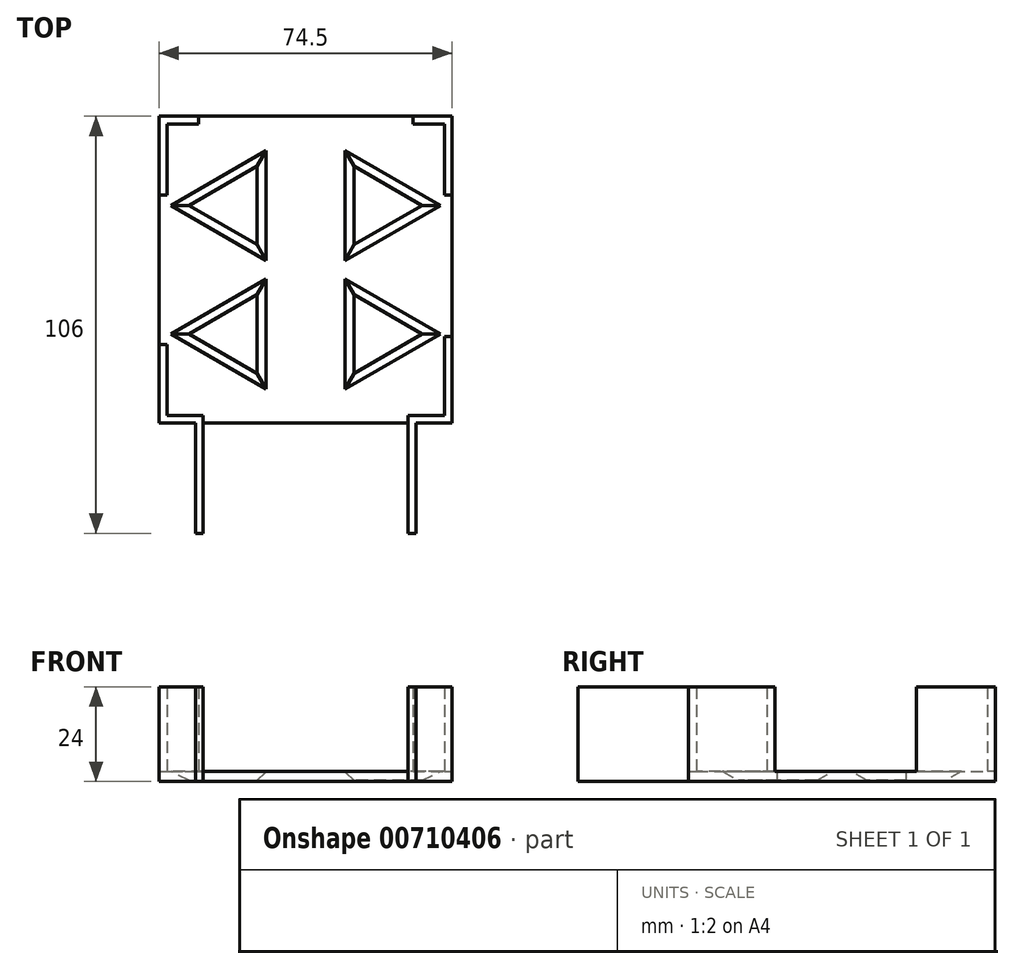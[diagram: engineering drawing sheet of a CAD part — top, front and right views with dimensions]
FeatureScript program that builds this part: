
annotation { "Feature Type Name" : "Feature", "Feature Type Description" : "" }
export const myFeature = defineFeature(function(context is Context, id is Id, definition is map)
    precondition{}
    {
        {
            var Q0;
            Q0=qCreatedBy(makeId("Top.planeOp"),FACE);
            var sketch = newSketch(context, id + "F0", { "sketchPlane" : qUnion([Q0])});
            skLineSegment(sketch, "E0.bottom", {"start": v(-37.25, -39) * mm, "end": v(37.25, -39) * mm});
            skLineSegment(sketch, "E0.top", {"start": v(-37.25, 39) * mm, "end": v(37.25, 39) * mm});
            skLineSegment(sketch, "E0.left", {"start": v(-37.25, -39) * mm, "end": v(-37.25, 39) * mm});
            skLineSegment(sketch, "E0.right", {"start": v(37.25, -39) * mm, "end": v(37.25, 39) * mm});
            skPoint(sketch, "E0.middle", {"position": v(0, 0) * mm});
            skLineSegment(sketch, "E1", {"start": v(0, -39) * mm, "end": v(0, 39) * mm});
            skLineSegment(sketch, "E2", {"start": v(29.62, 16.33) * mm, "end": v(12.3, 6.33) * mm});
            skLineSegment(sketch, "E3", {"start": v(12.3, 6.33) * mm, "end": v(12.3, 26.33) * mm});
            skLineSegment(sketch, "E4", {"start": v(12.3, 26.33) * mm, "end": v(29.62, 16.33) * mm});
            skLineSegment(sketch, "E5.MirrorCS", {"start": v(-12.3, 6.33) * mm, "end": v(-12.3, 26.33) * mm});
            skLineSegment(sketch, "E6.MirrorCS", {"start": v(-12.3, 26.33) * mm, "end": v(-29.62, 16.33) * mm});
            skLineSegment(sketch, "E7.MirrorCS", {"start": v(-29.62, 16.33) * mm, "end": v(-12.3, 6.33) * mm});
            skLineSegment(sketch, "E8.MirrorCS", {"start": v(-29.62, -16.33) * mm, "end": v(-12.3, -6.33) * mm});
            skLineSegment(sketch, "E9.MirrorCS", {"start": v(-12.3, -26.33) * mm, "end": v(-29.62, -16.33) * mm});
            skLineSegment(sketch, "E10.MirrorCS", {"start": v(-12.3, -6.33) * mm, "end": v(-12.3, -26.33) * mm});
            skLineSegment(sketch, "E11.MirrorCS", {"start": v(12.3, -6.33) * mm, "end": v(12.3, -26.33) * mm});
            skLineSegment(sketch, "E12.MirrorCS", {"start": v(12.3, -26.33) * mm, "end": v(29.62, -16.33) * mm});
            skLineSegment(sketch, "E13.MirrorCS", {"start": v(29.62, -16.33) * mm, "end": v(12.3, -6.33) * mm});
            skLineSegment(sketch, "E14", {"start": v(-35.25, 37) * mm, "end": v(35.25, 37) * mm});
            skLineSegment(sketch, "E15", {"start": v(35.25, 37) * mm, "end": v(35.25, -37) * mm});
            skLineSegment(sketch, "E16", {"start": v(35.25, -37) * mm, "end": v(-35.25, -37) * mm});
            skLineSegment(sketch, "E17", {"start": v(-35.25, -37) * mm, "end": v(-35.25, 37) * mm});
            skLineSegment(sketch, "E18", {"start": v(37.25, 39) * mm, "end": v(37.25, 19) * mm, "construction": true});
            skLineSegment(sketch, "E19", {"start": v(37.25, 19) * mm, "end": v(35.25, 19) * mm});
            skLineSegment(sketch, "E20", {"start": v(37.25, 39) * mm, "end": v(27.25, 39) * mm, "construction": true});
            skLineSegment(sketch, "E21", {"start": v(27.25, 39) * mm, "end": v(27.25, 37) * mm});
            skLineSegment(sketch, "E22", {"start": v(35.25, -37) * mm, "end": v(35.25, -17) * mm, "construction": true});
            skLineSegment(sketch, "E23", {"start": v(35.25, -17) * mm, "end": v(37.25, -17) * mm});
            skLineSegment(sketch, "E24", {"start": v(-37.25, 39) * mm, "end": v(-37.25, 19) * mm, "construction": true});
            skLineSegment(sketch, "E25", {"start": v(-37.25, 19) * mm, "end": v(-35.25, 19) * mm});
            skLineSegment(sketch, "E26", {"start": v(37.25, -39) * mm, "end": v(28, -39) * mm, "construction": true});
            skLineSegment(sketch, "E27", {"start": v(26, -39) * mm, "end": v(26, -37) * mm});
            skLineSegment(sketch, "E28", {"start": v(-37.25, -39) * mm, "end": v(-28, -39) * mm, "construction": true});
            skLineSegment(sketch, "E29", {"start": v(-26, -39) * mm, "end": v(-26, -37) * mm});
            skLineSegment(sketch, "E30", {"start": v(-37.25, -39) * mm, "end": v(-37.25, -19) * mm, "construction": true});
            skLineSegment(sketch, "E31", {"start": v(-37.25, -19) * mm, "end": v(-35.25, -19) * mm});
            skLineSegment(sketch, "E32", {"start": v(-37.25, 39) * mm, "end": v(-27.25, 39) * mm, "construction": true});
            skLineSegment(sketch, "E33", {"start": v(-27.25, 39) * mm, "end": v(-27.25, 37) * mm});
            skText(sketch, "E34", { "text": "Front", "fontName": "OpenSans-Italic.ttf"});
            skText(sketch, "E35", { "text": "Back", "fontName": "OpenSans-Italic.ttf"});
            skLineSegment(sketch, "E36", {"start": v(28, -39) * mm, "end": v(28, -67) * mm});
            skLineSegment(sketch, "E37", {"start": v(-28, -39) * mm, "end": v(-28, -67) * mm});
            skLineSegment(sketch, "E38", {"start": v(28, -67) * mm, "end": v(26, -67) * mm});
            skLineSegment(sketch, "E39", {"start": v(26, -67) * mm, "end": v(26, -39) * mm});
            skLineSegment(sketch, "E40", {"start": v(-28, -67) * mm, "end": v(-26, -67) * mm});
            skLineSegment(sketch, "E41", {"start": v(-26, -67) * mm, "end": v(-26, -39) * mm});
            const initialGuessF0  = {"E34": [-0.01968, 0.05832, 1, 0, 0.01165], "E35": [-0.01674, -0.07005, 1, 0, 0.0123]};
            skSetInitialGuess(sketch, initialGuessF0);
            skSolve(sketch);
        }
        {
            var Q0;
            Q0=makeQuery(id+"F0.imprint","IMPRINT",FACE,{"disambiguationData":[TD([[makeQuery(id+"F0.imprint","IMPRINT",EDGE,{"derivedFrom":sQuery(id+"F0.wireOp",EDGE,"E2")}),1.0]])]});
            var Q1;
            Q1=makeQuery(id+"F0.imprint","IMPRINT",FACE,{"disambiguationData":[TD([[makeQuery(id+"F0.imprint","IMPRINT",EDGE,{"derivedFrom":sQuery(id+"F0.wireOp",EDGE,"E5.MirrorCS")}),-1.0]])]});
            var Q2;
            {var subQ3=sQuery(id+"F0.wireOp",EDGE,"E29");Q2=makeQuery(id+"F0.imprint","IMPRINT",FACE,{"disambiguationData":[TD([[makeQuery(id+"F0.imprint","IMPRINT",EDGE,{"derivedFrom":subQ3}),-1.0]])]});}
            var Q3;
            {var subQ3=sQuery(id+"F0.wireOp",EDGE,"E27");Q3=makeQuery(id+"F0.imprint","IMPRINT",FACE,{"disambiguationData":[TD([[makeQuery(id+"F0.imprint","IMPRINT",EDGE,{"derivedFrom":subQ3}),1.0]])]});}
            var Q4;
            {var subQ3=sQuery(id+"F0.wireOp",EDGE,"E33");Q4=makeQuery(id+"F0.imprint","IMPRINT",FACE,{"disambiguationData":[TD([[makeQuery(id+"F0.imprint","IMPRINT",EDGE,{"derivedFrom":subQ3}),1.0]])]});}
            var Q5;
            {var subQ3=sQuery(id+"F0.wireOp",EDGE,"E21");Q5=makeQuery(id+"F0.imprint","IMPRINT",FACE,{"disambiguationData":[TD([[makeQuery(id+"F0.imprint","IMPRINT",EDGE,{"derivedFrom":subQ3}),-1.0]])]});}
            var Q6;
            {var subQ0=sQuery(id+"F0.wireOp",EDGE,"E19");Q6=makeQuery(id+"F0.imprint","IMPRINT",FACE,{"disambiguationData":[TD([[makeQuery(id+"F0.imprint","IMPRINT",EDGE,{"derivedFrom":subQ0}),1.0]])]});}
            var Q7;
            {var subQ0=sQuery(id+"F0.wireOp",EDGE,"E25");Q7=makeQuery(id+"F0.imprint","IMPRINT",FACE,{"disambiguationData":[TD([[makeQuery(id+"F0.imprint","IMPRINT",EDGE,{"derivedFrom":subQ0}),-1.0]])]});}
            extrude(context, id + "F1", {"entities" : qUnion([Q0, Q1, Q2, Q3, Q4, Q5, Q6, Q7]), "depth" : 2.5 * mm, "offsetDistance" : 25 * mm});
        }
        {
            var Q0;
            Q0=makeQuery(id+"F1.opExtrude","CAP_EDGE",EDGE,{"disambiguationData":[OSD([sQuery(id+"F0.wireOp",EDGE,"E8.MirrorCS")])],"isStart":false});
            var Q1;
            Q1=makeQuery(id+"F1.opExtrude","CAP_EDGE",EDGE,{"disambiguationData":[OSD([sQuery(id+"F0.wireOp",EDGE,"E9.MirrorCS")])],"isStart":false});
            var Q2;
            Q2=makeQuery(id+"F1.opExtrude","CAP_EDGE",EDGE,{"disambiguationData":[OSD([sQuery(id+"F0.wireOp",EDGE,"E10.MirrorCS")])],"isStart":false});
            var Q3;
            Q3=makeQuery(id+"F1.opExtrude","CAP_EDGE",EDGE,{"disambiguationData":[OSD([sQuery(id+"F0.wireOp",EDGE,"E13.MirrorCS")])],"isStart":false});
            var Q4;
            Q4=makeQuery(id+"F1.opExtrude","CAP_EDGE",EDGE,{"disambiguationData":[OSD([sQuery(id+"F0.wireOp",EDGE,"E11.MirrorCS")])],"isStart":false});
            var Q5;
            Q5=makeQuery(id+"F1.opExtrude","CAP_EDGE",EDGE,{"disambiguationData":[OSD([sQuery(id+"F0.wireOp",EDGE,"E12.MirrorCS")])],"isStart":false});
            var Q6;
            Q6=makeQuery(id+"F1.opExtrude","CAP_EDGE",EDGE,{"disambiguationData":[OSD([sQuery(id+"F0.wireOp",EDGE,"E4")])],"isStart":false});
            var Q7;
            Q7=makeQuery(id+"F1.opExtrude","CAP_EDGE",EDGE,{"disambiguationData":[OSD([sQuery(id+"F0.wireOp",EDGE,"E3")])],"isStart":false});
            var Q8;
            Q8=makeQuery(id+"F1.opExtrude","CAP_EDGE",EDGE,{"disambiguationData":[OSD([sQuery(id+"F0.wireOp",EDGE,"E2")])],"isStart":false});
            var Q9;
            Q9=makeQuery(id+"F1.opExtrude","CAP_EDGE",EDGE,{"disambiguationData":[OSD([sQuery(id+"F0.wireOp",EDGE,"E6.MirrorCS")])],"isStart":false});
            var Q10;
            Q10=makeQuery(id+"F1.opExtrude","CAP_EDGE",EDGE,{"disambiguationData":[OSD([sQuery(id+"F0.wireOp",EDGE,"E7.MirrorCS")])],"isStart":false});
            var Q11;
            Q11=makeQuery(id+"F1.opExtrude","CAP_EDGE",EDGE,{"disambiguationData":[OSD([sQuery(id+"F0.wireOp",EDGE,"E5.MirrorCS")])],"isStart":false});
            chamfer(context, id + "F2", {"entities" : qUnion([Q0, Q1, Q2, Q3, Q4, Q5, Q6, Q7, Q8, Q9, Q10, Q11]), "width" : 2.3 * mm, "tangentPropagation" : true});
        }
        {
            var Q0;
            {var subQ3=sQuery(id+"F0.wireOp",EDGE,"E25");Q0=makeQuery(id+"F0.imprint","IMPRINT",FACE,{"disambiguationData":[TD([[makeQuery(id+"F0.imprint","IMPRINT",EDGE,{"derivedFrom":subQ3}),1.0]])]});}
            var Q1;
            {var subQ3=sQuery(id+"F0.wireOp",EDGE,"E19");Q1=makeQuery(id+"F0.imprint","IMPRINT",FACE,{"disambiguationData":[TD([[makeQuery(id+"F0.imprint","IMPRINT",EDGE,{"derivedFrom":subQ3}),-1.0]])]});}
            var Q2;
            {var subQ3=sQuery(id+"F0.wireOp",EDGE,"E23");Q2=makeQuery(id+"F0.imprint","IMPRINT",FACE,{"disambiguationData":[TD([[makeQuery(id+"F0.imprint","IMPRINT",EDGE,{"derivedFrom":subQ3}),-1.0]])]});}
            var Q3;
            {var subQ3=sQuery(id+"F0.wireOp",EDGE,"E29");Q3=makeQuery(id+"F0.imprint","IMPRINT",FACE,{"disambiguationData":[TD([[makeQuery(id+"F0.imprint","IMPRINT",EDGE,{"derivedFrom":subQ3}),1.0]])]});}
            var Q4;
            {var subQ2=sQuery(id+"F0.wireOp",EDGE,"E36");Q4=makeQuery(id+"F0.imprint","IMPRINT",FACE,{"disambiguationData":[TD([[makeQuery(id+"F0.imprint","IMPRINT",EDGE,{"derivedFrom":subQ2}),-1.0]])]});}
            var Q5;
            {var subQ2=sQuery(id+"F0.wireOp",EDGE,"E37");Q5=makeQuery(id+"F0.imprint","IMPRINT",FACE,{"disambiguationData":[TD([[makeQuery(id+"F0.imprint","IMPRINT",EDGE,{"derivedFrom":subQ2}),1.0]])]});}
            extrude(context, id + "F3", {"entities" : qUnion([Q0, Q1, Q2, Q3, Q4, Q5]), "operationType" : NewBodyOperationType.ADD, "depth" : 24 * mm, "offsetDistance" : 25 * mm});
        }
    });
